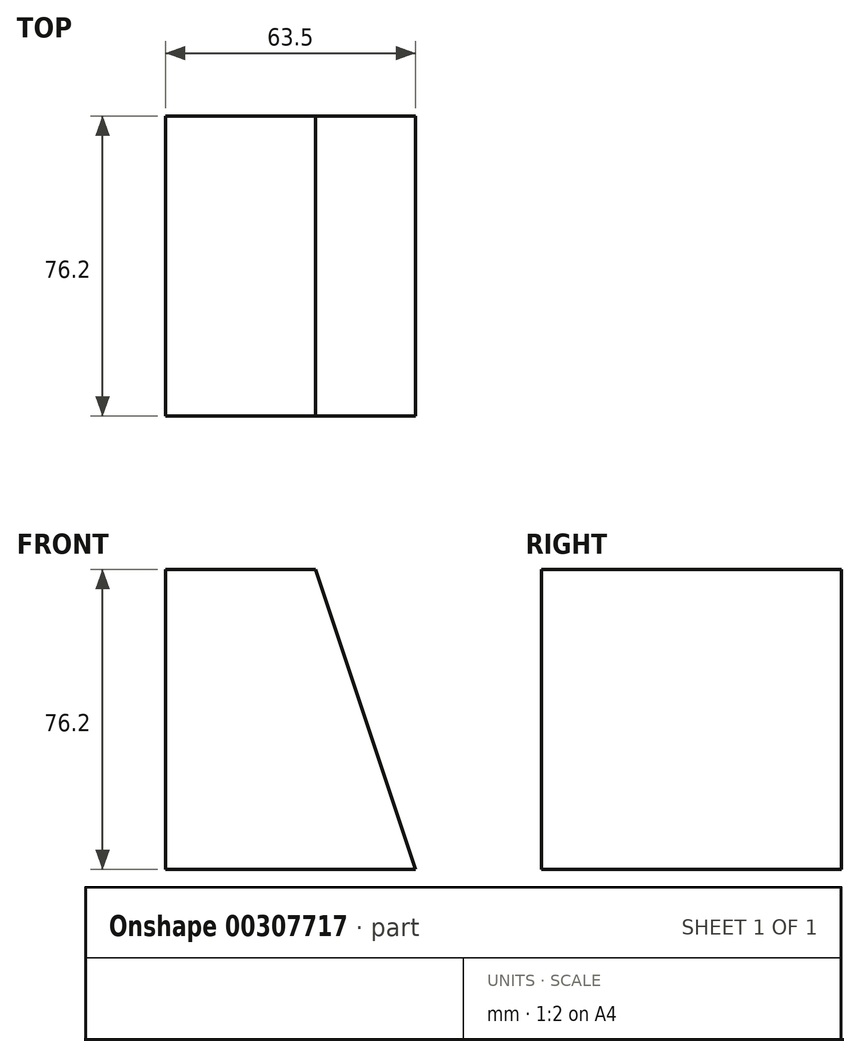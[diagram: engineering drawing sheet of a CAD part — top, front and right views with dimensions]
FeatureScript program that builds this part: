
annotation { "Feature Type Name" : "Feature", "Feature Type Description" : "" }
export const myFeature = defineFeature(function(context is Context, id is Id, definition is map)
    precondition{}
    {
        {
            var Q0;
            Q0=qCreatedBy(makeId("Front.planeOp"),FACE);
            var sketch = newSketch(context, id + "F0", { "sketchPlane" : qUnion([Q0])});
            skLineSegment(sketch, "E0", {"start": v(-30.82, -88.4) * mm, "end": v(32.68, -88.4) * mm});
            skLineSegment(sketch, "E1", {"start": v(32.68, -88.4) * mm, "end": v(7.28, -12.2) * mm});
            skLineSegment(sketch, "E2", {"start": v(7.28, -12.2) * mm, "end": v(-30.82, -12.2) * mm});
            skLineSegment(sketch, "E3", {"start": v(-30.82, -12.2) * mm, "end": v(-30.82, -88.4) * mm});
            skSolve(sketch);
        }
        {
            var Q0;
            Q0=makeQuery(id+"F0.imprint","IMPRINT",FACE,{"disambiguationData":[TD([[makeQuery(id+"F0.imprint","IMPRINT",EDGE,{"derivedFrom":sQuery(id+"F0.wireOp",EDGE,"E0")}),1.0]])]});
            extrude(context, id + "F1", {"entities" : qUnion([Q0]), "depth" : 76.2 * mm});
        }
    });
